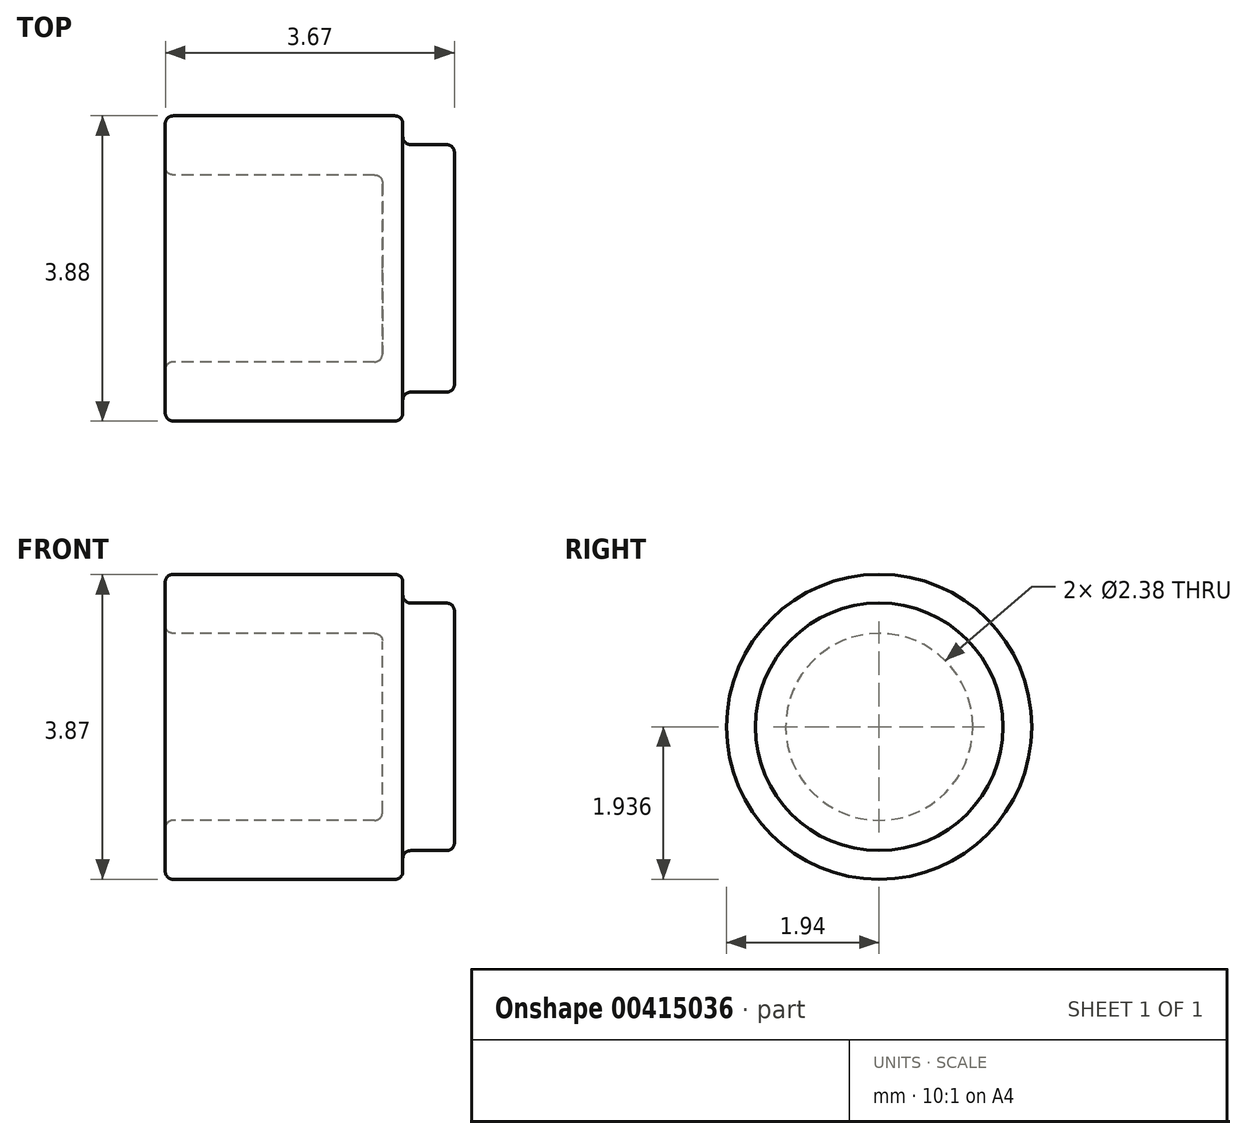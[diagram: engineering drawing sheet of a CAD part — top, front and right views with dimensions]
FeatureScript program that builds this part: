
annotation { "Feature Type Name" : "Feature", "Feature Type Description" : "" }
export const myFeature = defineFeature(function(context is Context, id is Id, definition is map)
    precondition{}
    {
        {
            var Q0;
            Q0=qCreatedBy(makeId("Front.planeOp"),FACE);
            var sketch = newSketch(context, id + "F0", { "sketchPlane" : qUnion([Q0])});
            skLineSegment(sketch, "E0.bottom", {"start": v(-13.67, 0.96) * mm, "end": v(11.33, 0.96) * mm});
            skLineSegment(sketch, "E0.top", {"start": v(-13.67, -0.04) * mm, "end": v(11.33, -0.04) * mm});
            skLineSegment(sketch, "E0.left", {"start": v(-13.67, 0.96) * mm, "end": v(-13.67, -0.04) * mm});
            skLineSegment(sketch, "E0.right", {"start": v(11.33, 0.96) * mm, "end": v(11.33, -0.04) * mm});
            skLineSegment(sketch, "E1", {"start": v(-13.67, -2.04) * mm, "end": v(11.33, -2.04) * mm});
            skLineSegment(sketch, "E2.bottom", {"start": v(5.05, -0.04) * mm, "end": v(4.8, -0.04) * mm});
            skLineSegment(sketch, "E2.top", {"start": v(5.05, -0.4) * mm, "end": v(4.8, -0.4) * mm});
            skLineSegment(sketch, "E2.left", {"start": v(5.05, -0.04) * mm, "end": v(5.05, -0.4) * mm});
            skLineSegment(sketch, "E2.right", {"start": v(4.8, -0.04) * mm, "end": v(4.8, -0.4) * mm});
            skArc(sketch, "E3", {"start": v(-13.67, -0.04) * mm, "mid": v(-13.1, -0.31) * mm, "end": v(-12.52, -0.04) * mm});
            skArc(sketch, "E4", {"start": v(1.73, 0.96) * mm, "mid": v(-0.77, 1.5) * mm, "end": v(-3.27, 0.96) * mm});
            skLineSegment(sketch, "E5.bottom", {"start": v(1.73, -0.1) * mm, "end": v(4.75, -0.1) * mm});
            skLineSegment(sketch, "E5.top", {"start": v(1.73, -0.86) * mm, "end": v(4.75, -0.86) * mm});
            skLineSegment(sketch, "E5.left", {"start": v(1.73, -0.1) * mm, "end": v(1.73, -0.86) * mm});
            skLineSegment(sketch, "E5.right", {"start": v(4.75, -0.1) * mm, "end": v(4.75, -0.88) * mm});
            skLineSegment(sketch, "E6.bottom", {"start": v(4.75, -0.47) * mm, "end": v(5.4, -0.47) * mm});
            skLineSegment(sketch, "E6.top", {"start": v(4.75, -2.04) * mm, "end": v(5.4, -2.04) * mm});
            skLineSegment(sketch, "E6.left", {"start": v(4.75, -0.47) * mm, "end": v(4.75, -2.04) * mm});
            skLineSegment(sketch, "E6.right", {"start": v(5.4, -0.47) * mm, "end": v(5.4, -2.04) * mm});
            skLineSegment(sketch, "E7.bottom", {"start": v(4.49, -0.86) * mm, "end": v(4.75, -0.86) * mm});
            skLineSegment(sketch, "E7.top", {"start": v(4.49, -2.04) * mm, "end": v(4.75, -2.04) * mm});
            skLineSegment(sketch, "E7.left", {"start": v(4.49, -0.86) * mm, "end": v(4.49, -2.04) * mm});
            skLineSegment(sketch, "E7.right", {"start": v(4.75, -0.86) * mm, "end": v(4.75, -2.04) * mm});
            skArc(sketch, "E8", {"start": v(5.4, -1.8) * mm, "mid": v(5.2, -1.88) * mm, "end": v(5.07, -2.04) * mm});
            skSolve(sketch);
        }
        {
            var Q0;
            {var subQ5=sQuery(id+"F0.wireOp",EDGE,"E5.bottom");Q0=makeQuery(id+"F0.imprint","IMPRINT",FACE,{"disambiguationData":[TD([[makeQuery(id+"F0.imprint","IMPRINT",EDGE,{"derivedFrom":subQ5}),-1.0]])]});}
            var Q1;
            {var subQ3=sQuery(id+"F0.wireOp",EDGE,"E6.bottom");Q1=makeQuery(id+"F0.imprint","IMPRINT",FACE,{"disambiguationData":[TD([[makeQuery(id+"F0.imprint","IMPRINT",EDGE,{"derivedFrom":subQ3}),-1.0]])]});}
            var Q2;
            {var subQ0=sQuery(id+"F0.wireOp",EDGE,"E6.left");Q2=makeQuery(id+"F0.imprint","IMPRINT",FACE,{"disambiguationData":[TD([[makeQuery(id+"F0.imprint","IMPRINT",EDGE,{"derivedFrom":subQ0}),-1.0]])]});}
            var Q3;
            {var subQ3=sQuery(id+"F0.wireOp",EDGE,"E8");Q3=makeQuery(id+"F0.imprint","IMPRINT",FACE,{"disambiguationData":[TD([[makeQuery(id+"F0.imprint","IMPRINT",EDGE,{"derivedFrom":subQ3}),1.0]])]});}
            var Q4;
            Q4=sQuery(id+"F0.wireOp",EDGE,"E1");
            revolve(context, id + "F1", {"entities" : qUnion([Q0, Q1, Q2, Q3]), "axis" : qUnion([Q4]), "revolveType" : RevolveType.FULL});
        }
        {
            var Q0;
            Q0=makeQuery(id+"F1.opRevolve","SWEPT_EDGE",EDGE,{"disambiguationData":[OSD([sQuery(id+"F0.wireOp",EDGE,"E5.right"),sQuery(id+"F0.wireOp",EDGE,"E6.bottom")])]});
            var Q1;
            Q1=makeQuery(id+"F1.opRevolve","SWEPT_EDGE",EDGE,{"disambiguationData":[OSD([sQuery(id+"F0.wireOp",EDGE,"E6.bottom"),sQuery(id+"F0.wireOp",EDGE,"E6.right")])]});
            var Q2;
            Q2=makeQuery(id+"F1.opRevolve","SWEPT_EDGE",EDGE,{"disambiguationData":[OSD([sQuery(id+"F0.wireOp",EDGE,"E5.bottom"),sQuery(id+"F0.wireOp",EDGE,"E5.left")])]});
            var Q3;
            Q3=makeQuery(id+"F1.opRevolve","SWEPT_EDGE",EDGE,{"disambiguationData":[OSD([sQuery(id+"F0.wireOp",EDGE,"E5.top"),sQuery(id+"F0.wireOp",EDGE,"E5.left")])]});
            var Q4;
            Q4=makeQuery(id+"F1.opRevolve","SWEPT_EDGE",EDGE,{"disambiguationData":[OSD([sQuery(id+"F0.wireOp",EDGE,"E5.top"),sQuery(id+"F0.wireOp",EDGE,"E7.left")])]});
            var Q5;
            Q5=makeQuery(id+"F1.opRevolve","SWEPT_EDGE",EDGE,{"disambiguationData":[OSD([sQuery(id+"F0.wireOp",EDGE,"E5.bottom"),sQuery(id+"F0.wireOp",EDGE,"E5.right")])]});
            fillet(context, id + "F2", {"entities" : qUnion([Q0, Q1, Q2, Q3, Q4, Q5]), "radius" : 0.1 * mm, "tangentPropagation" : true, "allowEdgeOverflow" : false});
        }
    });
